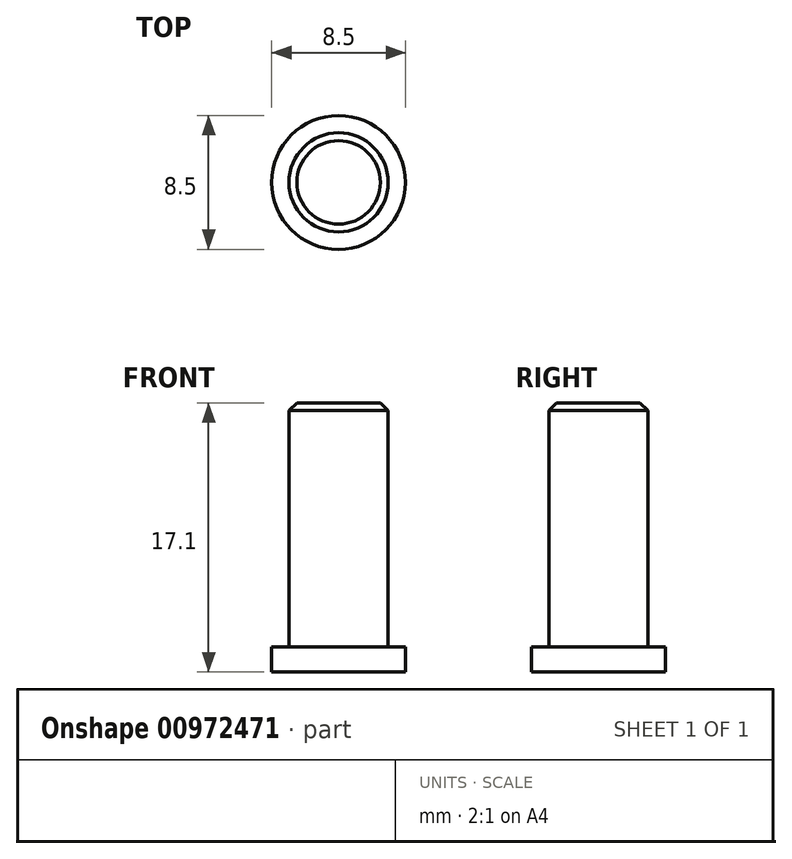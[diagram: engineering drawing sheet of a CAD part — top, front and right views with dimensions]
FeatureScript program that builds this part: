
annotation { "Feature Type Name" : "Feature", "Feature Type Description" : "" }
export const myFeature = defineFeature(function(context is Context, id is Id, definition is map)
    precondition{}
    {
        {
            var Q0;
            Q0=qCreatedBy(makeId("Top.planeOp"),FACE);
            var sketch = newSketch(context, id + "F0", { "sketchPlane" : qUnion([Q0])});
            skCircle(sketch, "E0", {"center": v(0, 0) * mm, "radius": 4.25 * mm});
            skSolve(sketch);
        }
        {
            var Q0;
            Q0 = qSketchRegion(id + "F0", true);
            extrude(context, id + "F1", {"entities" : qUnion([Q0]), "depth" : 1.6 * mm, "offsetDistance" : 25 * mm});
        }
        {
            var Q0;
            Q0=makeQuery(id+"F1.opExtrude","CAP_FACE",FACE,{"disambiguationData":[OSD([sQuery(id+"F0.wireOp",EDGE,"E0")])],"isStart":false});
            var sketch = newSketch(context, id + "F2", { "sketchPlane" : qUnion([Q0])});
            skCircle(sketch, "E1", {"center": v(0, 0) * mm, "radius": 3.15 * mm});
            skSolve(sketch);
        }
        {
            var Q0;
            Q0 = qSketchRegion(id + "F2", true);
            extrude(context, id + "F3", {"entities" : qUnion([Q0]), "operationType" : NewBodyOperationType.ADD, "depth" : 15.5 * mm, "offsetDistance" : 25 * mm});
        }
        {
            var Q0;
            Q0=makeQuery(id+"F3.opExtrude","CAP_FACE",FACE,{"disambiguationData":[OSD([sQuery(id+"F2.wireOp",EDGE,"E1")])],"isStart":false});
            chamfer(context, id + "F4", {"entities" : qUnion([Q0]), "width" : .5 * mm, "tangentPropagation" : true});
        }
    });
